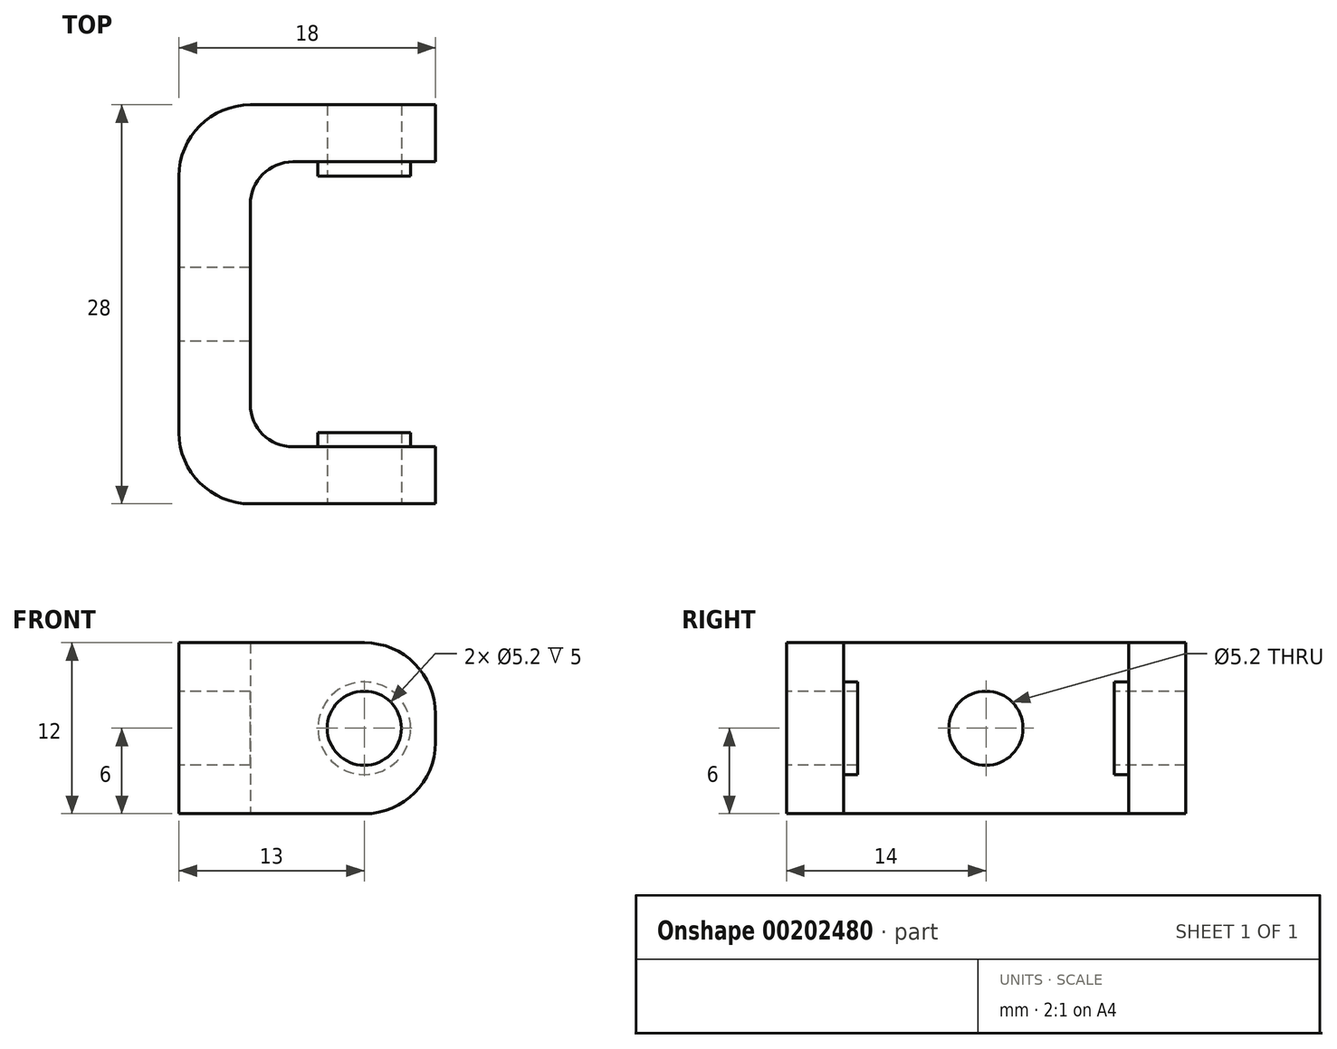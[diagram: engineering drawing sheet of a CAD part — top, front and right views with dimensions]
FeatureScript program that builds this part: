
annotation { "Feature Type Name" : "Feature", "Feature Type Description" : "" }
export const myFeature = defineFeature(function(context is Context, id is Id, definition is map)
    precondition{}
    {
        {
            var Q0;
            Q0=qCreatedBy(makeId("Top.planeOp"),FACE);
            var sketch = newSketch(context, id + "F0", { "sketchPlane" : qUnion([Q0])});
            skLineSegment(sketch, "E0.bottom", {"start": v(-8, 14) * mm, "end": v(5, 14) * mm});
            skLineSegment(sketch, "E0.left", {"start": v(-13, 9) * mm, "end": v(-13, -9) * mm});
            skLineSegment(sketch, "E1", {"start": v(5, 14) * mm, "end": v(5, 10) * mm});
            skLineSegment(sketch, "E2", {"start": v(5, 10) * mm, "end": v(-5, 10) * mm});
            skLineSegment(sketch, "E3", {"start": v(-8, 7) * mm, "end": v(-8, -7) * mm});
            skLineSegment(sketch, "E4", {"start": v(-5, -10) * mm, "end": v(5, -10) * mm});
            skLineSegment(sketch, "E5", {"start": v(5, -10) * mm, "end": v(5, -14) * mm});
            skPoint(sketch, "E6.visualSharp", {"position": v(-8, 10) * mm});
            skArc(sketch, "E6.filletArc", {"start": v(-5, 10) * mm, "mid": v(-7.12, 9.12) * mm, "end": v(-8, 7) * mm});
            skPoint(sketch, "E7.visualSharp", {"position": v(-8, -10) * mm});
            skArc(sketch, "E7.filletArc", {"start": v(-8, -7) * mm, "mid": v(-7.12, -9.12) * mm, "end": v(-5, -10) * mm});
            skLineSegment(sketch, "E8", {"start": v(-8, -14) * mm, "end": v(5, -14) * mm});
            skPoint(sketch, "E9.visualSharp", {"position": v(-13, 14) * mm});
            skArc(sketch, "E9.filletArc", {"start": v(-8, 14) * mm, "mid": v(-11.54, 12.54) * mm, "end": v(-13, 9) * mm});
            skPoint(sketch, "E10.visualSharp", {"position": v(-13, -14) * mm});
            skArc(sketch, "E10.filletArc", {"start": v(-13, -9) * mm, "mid": v(-11.54, -12.54) * mm, "end": v(-8, -14) * mm});
            skSolve(sketch);
        }
        {
            var Q0;
            Q0=qSketchRegion(id+"F0",true);
            extrude(context, id + "F1", {"entities" : qUnion([Q0]), "depth" : 6 * mm, "hasSecondDirection" : true, "secondDirectionOppositeDirection" : true, "secondDirectionDepth" : 6 * mm});
        }
        {
            var Q0;
            Q0=makeQuery(id+"F1.opExtrude","SWEPT_FACE",FACE,{"disambiguationData":[OSD([sQuery(id+"F0.wireOp",EDGE,"E0.left")])]});
            var sketch = newSketch(context, id + "F2", { "sketchPlane" : qUnion([Q0])});
            skCircle(sketch, "E11", {"center": v(0, 0) * mm, "radius": 2.6 * mm});
            skSolve(sketch);
        }
        {
            var Q0;
            Q0=qSketchRegion(id+"F2",true);
            extrude(context, id + "F3", {"entities" : qUnion([Q0]), "operationType" : NewBodyOperationType.REMOVE, "endBound" : BoundingType.UP_TO_NEXT, "oppositeDirection" : true, "depth" : 25 * mm});
        }
        {
            var Q0;
            Q0=qCreatedBy(makeId("Front.planeOp"),FACE);
            var sketch = newSketch(context, id + "F4", { "sketchPlane" : qUnion([Q0])});
            skCircle(sketch, "E12", {"center": v(0, 0) * mm, "radius": 2.6 * mm});
            skSolve(sketch);
        }
        {
            var Q0;
            Q0=qSketchRegion(id+"F4",true);
            extrude(context, id + "F5", {"entities" : qUnion([Q0]), "operationType" : NewBodyOperationType.REMOVE, "endBound" : BoundingType.THROUGH_ALL, "oppositeDirection" : true, "depth" : 25 * mm, "hasSecondDirection" : true, "secondDirectionBound" : SecondDirectionBoundingType.THROUGH_ALL, "secondDirectionOppositeDirection" : false, "secondDirectionDepth" : 25 * mm});
        }
        {
            var Q0;
            Q0=makeQuery(id+"F1.opExtrude","CAP_EDGE",EDGE,{"disambiguationData":[OSD([sQuery(id+"F0.wireOp",EDGE,"E5")])],"isStart":false});
            var Q1;
            Q1=makeQuery(id+"F1.opExtrude","CAP_EDGE",EDGE,{"disambiguationData":[OSD([sQuery(id+"F0.wireOp",EDGE,"E5")])],"isStart":true});
            var Q2;
            Q2=makeQuery(id+"F1.opExtrude","CAP_EDGE",EDGE,{"disambiguationData":[OSD([sQuery(id+"F0.wireOp",EDGE,"E1")])],"isStart":true});
            var Q3;
            Q3=makeQuery(id+"F1.opExtrude","CAP_EDGE",EDGE,{"disambiguationData":[OSD([sQuery(id+"F0.wireOp",EDGE,"E1")])],"isStart":false});
            fillet(context, id + "F6", {"entities" : qUnion([Q0, Q1, Q2, Q3]), "radius" : 5 * mm, "tangentPropagation" : true, "allowEdgeOverflow" : false});
        }
        {
            var Q0;
            Q0=makeQuery(id+"F1.opExtrude","SWEPT_FACE",FACE,{"disambiguationData":[OSD([sQuery(id+"F0.wireOp",EDGE,"E2")])]});
            var sketch = newSketch(context, id + "F7", { "sketchPlane" : qUnion([Q0])});
            skCircle(sketch, "E13.1", {"center": v(0, 0) * mm, "radius": 2.6 * mm});
            skCircle(sketch, "E14.0", {"center": v(0, 0) * mm, "radius": 3.25 * mm});
            skSolve(sketch);
        }
        {
            var Q0;
            Q0=qSketchRegion(id+"F7",true);
            extrude(context, id + "F8", {"entities" : qUnion([Q0]), "depth" : 1 * mm});
        }
        {
            var Q0;
            Q0=makeQuery(id+"F8.opExtrude","SWEPT_BODY",BODY,{"disambiguationData":[OSD([sQuery(id+"F7.wireOp",EDGE,"E13.1"),sQuery(id+"F7.wireOp",EDGE,"E14.0")])]});
            var Q1;
            Q1=qCreatedBy(makeId("Front.planeOp"),FACE);
            mirror(context, id + "F9", {"operationType" : NewBodyOperationType.ADD, "entities" : qUnion([Q0]), "mirrorPlane" : qUnion([Q1])});
        }
    });
